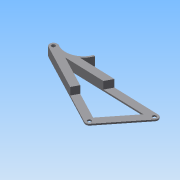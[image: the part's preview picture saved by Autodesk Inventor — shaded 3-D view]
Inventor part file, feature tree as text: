
AUTODESK INVENTOR PART (.ipt)
format: ipt  version: 2015 (Build 190159000, 159)  size: 178,688 bytes
history: native  units: mm
features: sketch x9, extrude x7, other x3
ambient origin geometry x8: Origin, YZ Plane, XZ Plane, XY Plane, X Axis, Y Axis, Z Axis, Center Point
bodies: Body1 (feature_tree)
feature tree (19):
  other  "實體1"
  extrude  "擠出1"  Depth=28.86mm
  extrude  "擠出2"  Depth=35.28mm
  extrude  "擠出3"  Depth=15.61mm
  extrude  "擠出4"  Depth=2.5mm
  extrude  "擠出5"  Depth=2.5mm
  extrude  "擠出6"  Depth=2.5mm
  extrude  "擠出7"  Depth=2.0mm TaperAngle=0.0deg
  other  "迴轉2"
  other  "迴轉1"
  sketch  "草圖1"
  sketch  "草圖2"
  sketch  "草圖3"
  sketch  "草圖4"
  sketch  "草圖5"
  sketch  "草圖6"
  sketch  "草圖7"
  sketch  "草圖8"
  sketch  "草圖9"
